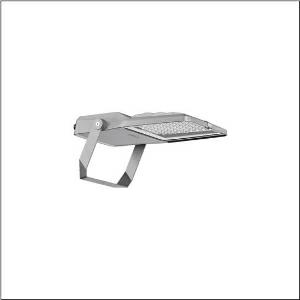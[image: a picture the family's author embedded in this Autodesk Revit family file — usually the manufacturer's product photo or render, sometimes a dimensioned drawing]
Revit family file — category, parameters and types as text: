
# Revit family: floodlight_fl_21_mini___pl43_5xa7776b4a1a_dd59
name_source: partatom
category: Lighting Fixtures
units: mm (PartAtom-declared; Revit-internal decimal feet)

## family parameters
Cut with Voids When Loaded = No
Host = Face
Light Source = No
Part Type = Normal
Room Calculation Point = No
Round Connector Dimension = Use Diameter
Shared = No

## types (1)
- --- (1 x LED, 6650 lm, 45.7 W, 4000K)
    Apparent Load = 46 VA
    CIE Flux Codes = 27 78 99 100 100
    Color Rendering = 70
    Color Temperature = 4000K
    Default Elevation = 1800 mm
    Description = Floodlight FL 21 mini, floodlight, primary light control with lens, of PMMA, primary optical cover: protective disc, of toughened safety glass, transparent, light distribution: PL43, light emission: direct distribution, installation type: surface-mounted, LED, High Power LED, rated luminous flux: 6.650lm, luminous efficacy: 146lm/W, light colour: 740, colour temperature: 4000K, control gear: D4iSmart Interface (Zhaga), control: overheat protection, constant luminous flux control, time-dependent luminous flux control, flexible luminous flux parameterisation, pre-setting: logarithmic dimming characteristic, with terminal, 6-pole, mains connection: 220..240V, AC, 50/60Hz, start of lifetime: 46W, end of service life: 48W, reduction: 22W, mounting bracket, of diecast aluminium, powder-coated, SITECO metallic grey (DB 702S), corrosivity category C5 mid according to DIN EN ISO 12944, suitable for swimming pools, chlorine-resistant, sealing non-destructively replaceable, mounting bracket, of steel, galvanised, powder-coated, SITECO metallic grey (DB 702S), Smart Interface below and above, protection rating (complete): IP66, insulation class (complete): insulation class II (safety insulation), certification: CE, ENEC, VDE, protection symbol: D, impact resistance: IK08, permissible operating ambient temperature: -40..+40°C, permissible operating ambient temperature for outdoor applications: -40..+50°C, standard: DIN EN 12944, LABS conformity tested according to VDMA 24364:2018-05, packaging unit: 1 piece

Light Distribution: PL43
    Height = 70 mm
    Lamp = 1 x LED
    Lamp Light Flux = 6650 lm
    Lamp Power = 45.7 W
    Lamp count = 1
    Length = 485 mm
    Luminous efficacy = 146 lm/W
    Manufacturer = Siteco
    ModVariant = No
    Model = 5XA7776B4A1A
    Number of Poles = 1
    OnlyDefault = Yes
    Power Factor = 1
    Product Name = Floodlight FL 21 mini | PL43
    Product group = floodlight | pylon annexe
    ProductGroupID = 6201
    Protection Class = Protection class II
    Protection Degree = IP 66
    RLX_Detail_Level = 1
    RLX_Emergency_Light_Flux = 0 lm
    RLX_Emergency_Type = 0
    RLX_Emergency_Type_DB = No
    RlxData = <blob elided: 95893 chars, md5=40c76b95>
    Socket = socket
    Standby Power = 0 W
    System Light Flux = 6650 lm
    System Power = 46 W
    Type Comments = factory setting: luminous flux: 100 % | dim-lin: 254 | 463 mA
    Type Image = l_1006845.jpg
    URL = http://relux.com
    VarID = @adj_099231
    Voltage = 0 V
    Weight = 0.00 kg
    Width = 337 mm

## geometry (parser evidence)
native form markers: Blend x4, Sweep x10
no freeform markers — native parametric forms only
